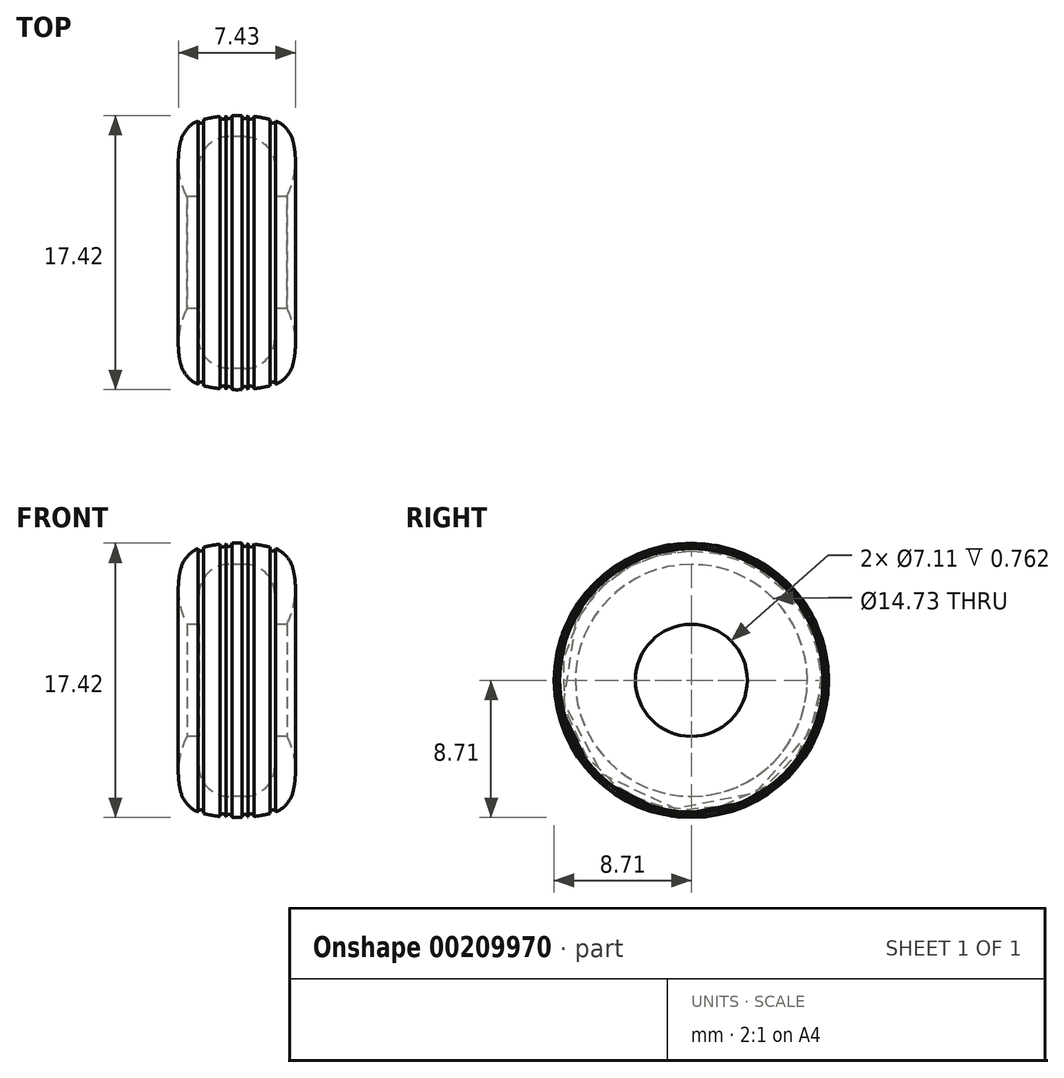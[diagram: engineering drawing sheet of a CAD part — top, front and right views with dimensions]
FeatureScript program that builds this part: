
annotation { "Feature Type Name" : "Feature", "Feature Type Description" : "" }
export const myFeature = defineFeature(function(context is Context, id is Id, definition is map)
    precondition{}
    {
        {
            var Q0;
            Q0=qCreatedBy(makeId("Front.planeOp"),FACE);
            var sketch = newSketch(context, id + "F0", { "sketchPlane" : qUnion([Q0])});
            skLineSegment(sketch, "E0", {"start": v(3.8, 3.56) * mm, "end": v(3.05, 3.56) * mm});
            skLineSegment(sketch, "E1", {"start": v(3.05, 3.56) * mm, "end": v(3.05, 7.37) * mm});
            skLineSegment(sketch, "E2", {"start": v(3.05, 7.37) * mm, "end": v(-1.78, 7.37) * mm});
            skLineSegment(sketch, "E3", {"start": v(-1.78, 7.37) * mm, "end": v(-1.78, 3.56) * mm});
            skLineSegment(sketch, "E4", {"start": v(-1.78, 3.56) * mm, "end": v(-2.54, 3.56) * mm});
            skArc(sketch, "E5", {"start": v(3.8, 8.13) * mm, "mid": v(0.63, 8.71) * mm, "end": v(-2.54, 8.13) * mm});
            skArc(sketch, "E6", {"start": v(-2.54, 8.13) * mm, "mid": v(-3.08, 5.84) * mm, "end": v(-2.54, 3.56) * mm});
            skArc(sketch, "E7", {"start": v(3.8, 3.56) * mm, "mid": v(4.35, 5.84) * mm, "end": v(3.8, 8.13) * mm});
            skLineSegment(sketch, "E8", {"start": v(-4.45, 0) * mm, "end": v(4.45, 0) * mm});
            skCircle(sketch, "E9", {"center": v(-1.65, 8.42) * mm, "radius": 0.2 * mm});
            skCircle(sketch, "E10", {"center": v(-0.25, 8.67) * mm, "radius": 0.2 * mm});
            skCircle(sketch, "E11", {"center": v(1.14, 8.7) * mm, "radius": 0.2 * mm});
            skCircle(sketch, "E12", {"center": v(0.13, 8.7) * mm, "radius": 0.2 * mm});
            skCircle(sketch, "E13", {"center": v(1.52, 8.67) * mm, "radius": 0.2 * mm});
            skCircle(sketch, "E14", {"center": v(2.92, 8.42) * mm, "radius": 0.2 * mm});
            skSolve(sketch);
        }
        {
            var Q0;
            Q0=makeQuery(id+"F0.imprint","IMPRINT",FACE,{"disambiguationData":[TD([[makeQuery(id+"F0.imprint","IMPRINT",EDGE,{"derivedFrom":sQuery(id+"F0.wireOp",EDGE,"E0")}),-1.0]])]});
            var Q1;
            Q1=sQuery(id+"F0.wireOp",EDGE,"E8");
            revolve(context, id + "F1", {"entities" : qUnion([Q0]), "axis" : qUnion([Q1]), "revolveType" : RevolveType.FULL});
        }
        {
            var Q0;
            Q0=makeQuery(id+"F1.opRevolve","SWEPT_EDGE",EDGE,{"disambiguationData":[OSD([sQuery(id+"F0.wireOp",EDGE,"E5"),sQuery(id+"F0.wireOp",EDGE,"E7")])]});
            var Q1;
            Q1=makeQuery(id+"F1.opRevolve","SWEPT_EDGE",EDGE,{"disambiguationData":[OSD([sQuery(id+"F0.wireOp",EDGE,"E5"),sQuery(id+"F0.wireOp",EDGE,"E6")])]});
            var Q2;
            Q2=makeQuery(id+"F1.opRevolve","SWEPT_EDGE",EDGE,{"disambiguationData":[OSD([sQuery(id+"F0.wireOp",EDGE,"E1"),sQuery(id+"F0.wireOp",EDGE,"E2")])]});
            var Q3;
            Q3=makeQuery(id+"F1.opRevolve","SWEPT_EDGE",EDGE,{"disambiguationData":[OSD([sQuery(id+"F0.wireOp",EDGE,"E2"),sQuery(id+"F0.wireOp",EDGE,"E3")])]});
            fillet(context, id + "F2", {"entities" : qUnion([Q0, Q1, Q2, Q3]), "radius" : 1.9 * mm, "tangentPropagation" : true, "allowEdgeOverflow" : false});
        }
    });
